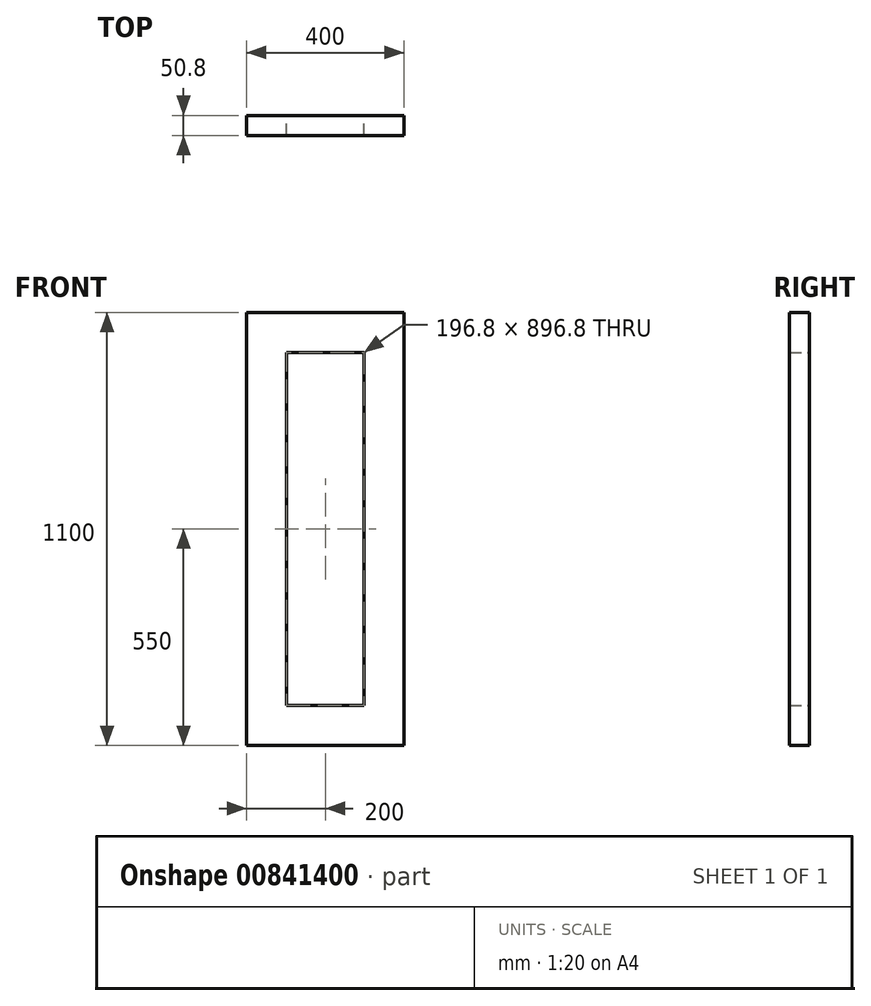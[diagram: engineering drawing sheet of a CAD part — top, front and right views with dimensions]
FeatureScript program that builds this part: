
annotation { "Feature Type Name" : "Feature", "Feature Type Description" : "" }
export const myFeature = defineFeature(function(context is Context, id is Id, definition is map)
    precondition{}
    {
        {
            var Q0;
            Q0=qCreatedBy(makeId("Front.planeOp"),FACE);
            var sketch = newSketch(context, id + "F0", { "sketchPlane" : qUnion([Q0])});
            skLineSegment(sketch, "E0.bottom", {"start": v(0, 0) * mm, "end": v(400, 0) * mm});
            skLineSegment(sketch, "E0.top", {"start": v(0, 1100) * mm, "end": v(400, 1100) * mm});
            skLineSegment(sketch, "E0.left", {"start": v(0, 0) * mm, "end": v(0, 1100) * mm});
            skLineSegment(sketch, "E0.right", {"start": v(400, 0) * mm, "end": v(400, 1100) * mm});
            skLineSegment(sketch, "E1.bottom", {"start": v(101.6, 998.4) * mm, "end": v(298.4, 998.4) * mm});
            skLineSegment(sketch, "E1.top", {"start": v(101.6, 101.6) * mm, "end": v(298.4, 101.6) * mm});
            skLineSegment(sketch, "E1.left", {"start": v(101.6, 998.4) * mm, "end": v(101.6, 101.6) * mm});
            skLineSegment(sketch, "E1.right", {"start": v(298.4, 998.4) * mm, "end": v(298.4, 101.6) * mm});
            skSolve(sketch);
        }
        {
            var Q0;
            Q0=makeQuery(id+"F0.imprint","IMPRINT",FACE,{"disambiguationData":[TD([[makeQuery(id+"F0.imprint","IMPRINT",EDGE,{"derivedFrom":sQuery(id+"F0.wireOp",EDGE,"E0.bottom")}),1.0]])]});
            extrude(context, id + "F1", {"entities" : qUnion([Q0]), "depth" : 50.8 * mm, "offsetDistance" : 25 * mm});
        }
    });
